# Revit family: KEUCO_14963010002
name_source: partatom
category: Sonderausstattung
revit_build: Autodesk Revit 2016 (Build: 20150220_1215(x64)
units: mm (PartAtom-declared; Revit-internal decimal feet)

## family parameters
Arbeitsebenenbasiert = Nein
Beim Laden mit Abzugskörper schneiden = Nein
Bemaßung runder Anschluss = Durchmesser verwenden
Gemeinsam genutzt = Nein
Immer vertikal = Ja
Raumberechnungspunkt = Nein
Teiletyp = Normal

## types (3) — shared parameters
Beschreibung = vertikale Ausführung,
für 2 Toilettenpapierrollen (Rollenbreite 100/120 mm)
Gewicht = 382
Hersteller = KEUCO
Kategorie = ACC
Preisgruppe = 1
Serie = Plan
URL = https://www.keuco.com
Verwendung = GWC / WC

## per-type parameters (varying)
| type | Ausschreibungstext |
| 14963010002 | KEUCO PLAN Toilettenpapier-Ersatzrollenhalter 2-fach, 14963010002
hochglanzverchromter Toilettenpapier-Ersatzrollenhalter 
zur Aufnahme von 2 WC-Papierrollen,
Rollenbreite 100/120 mm,
in ästhetischem, funktionalem Design
zur senkrechten Wandmontage, mit rechteckiger Wandbefestigung,
Rohrdurchmesser 25mm, leicht zu reinigen,
Ausladung waagerecht 66 mm, freie Rohrlänge 251 mm, Gesamthöhe 297 mm,
der Toilettenpapier-Ersatzrollenhalter wird verdeckt angebracht,
Lieferung inkl. korrosionsfreiem Befestigungsmaterial |
| 14963070002 | KEUCO PLAN Toilettenpapier-Ersatzrollenhalter 2-fach, 14963070002
Toilettenpapier-Ersatzrollenhalter aus hochwertigem Edelstahl 
zur Aufnahme von 2 WC-Papierrollen,
Rollenbreite 100/120 mm
in ästhetischem, funktionalem Design
zur senkrechten Wandmontage, mit rechteckiger Wandbefestigung,
Rohrdurchmesser 25mm, leicht zu reinigen,
Ausladung waagerecht 66 mm, freie Rohrlänge 251 mm, Gesamthöhe 297 mm,
der Toilettenpapier-Ersatzrollenhalter wird verdeckt angebracht,
Lieferung inkl. korrosionsfreiem Befestigungsmaterial |
| 14963170002 | KEUCO PLAN Toilettenpapier-Ersatzrollenhalter 2-fach, 14963170002
Toilettenpapier-Ersatzrollenhalter aus silber-eloxiertem Aluminium (E6 EV1)/verchromt
zur Aufnahme von 2 WC-Papierrollen,
Rollenbreite 100/120 mm
in ästhetischem, funktionalem Design
zur senkrechten Wandmontage, mit rechteckiger Wandbefestigung,
Rohrdurchmesser 25mm, leicht zu reinigen,
Ausladung waagerecht 66 mm, freie Rohrlänge 251 mm, Gesamthöhe 297 mm,
der Toilettenpapier-Ersatzrollenhalter wird verdeckt angebracht,
Lieferung inkl. korrosionsfreiem Befestigungsmaterial |

note: column(s) folded — value = type name in every type: Artikelnummer

## geometry (parser evidence)
native form markers: Blend x2, Sweep x3
no freeform markers — native parametric forms only
